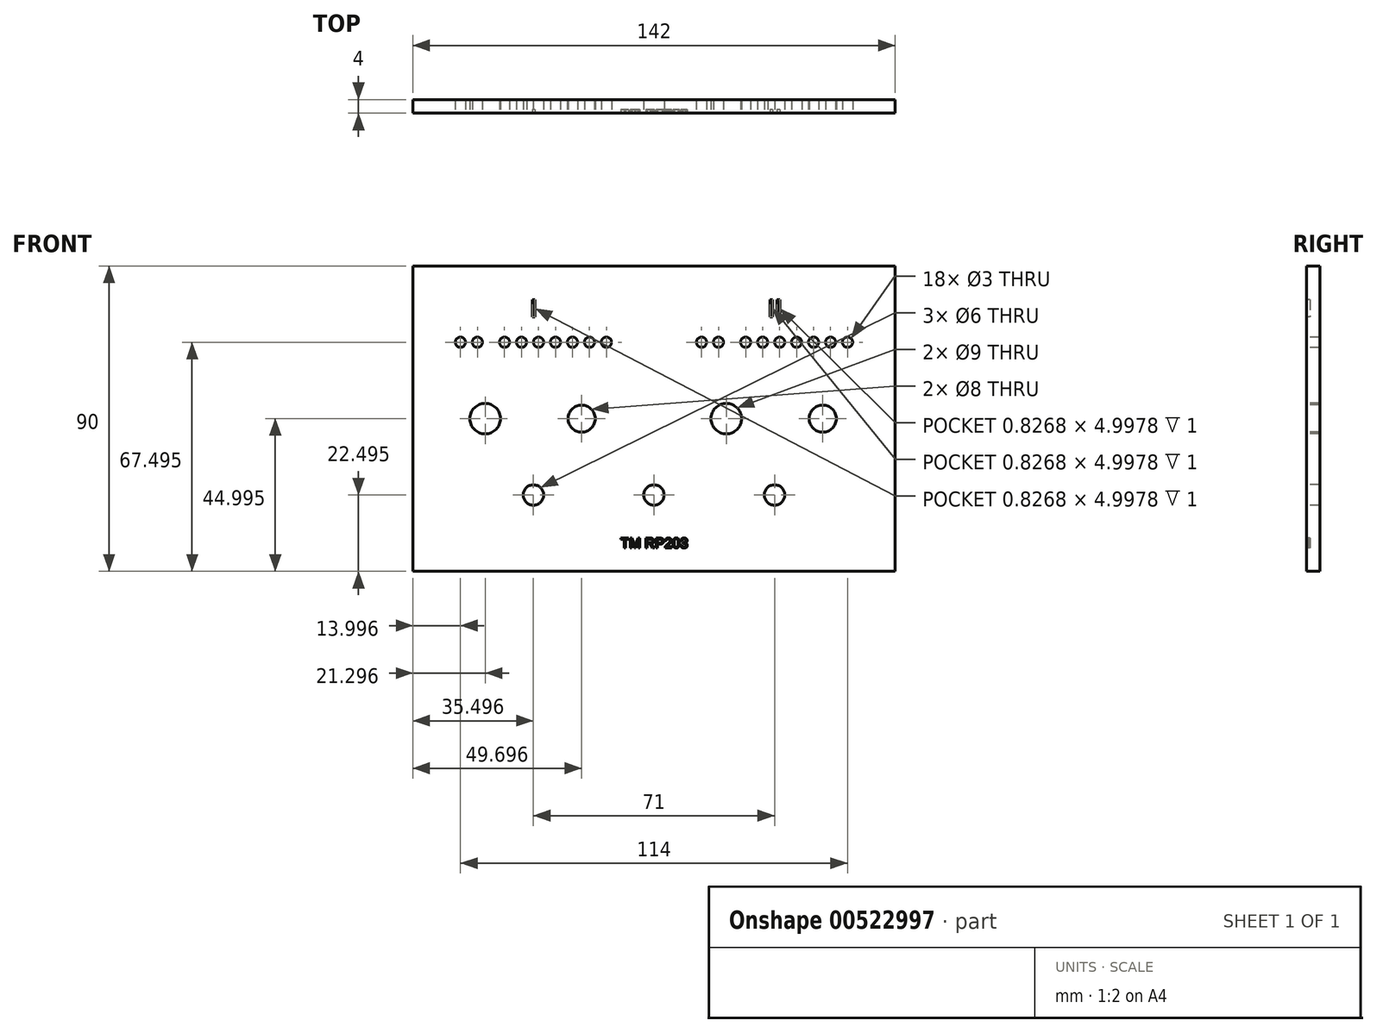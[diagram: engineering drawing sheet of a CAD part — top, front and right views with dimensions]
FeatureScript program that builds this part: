
annotation { "Feature Type Name" : "Feature", "Feature Type Description" : "" }
export const myFeature = defineFeature(function(context is Context, id is Id, definition is map)
    precondition{}
    {
        {
            var Q0;
            Q0=qCreatedBy(makeId("Front.planeOp"),FACE);
            var sketch = newSketch(context, id + "F0", { "sketchPlane" : qUnion([Q0])});
            skLineSegment(sketch, "E0.bottom", {"start": v(-71.11, 45.76) * mm, "end": v(70.89, 45.76) * mm});
            skLineSegment(sketch, "E0.top", {"start": v(-71.11, -44.24) * mm, "end": v(70.89, -44.24) * mm});
            skLineSegment(sketch, "E0.left", {"start": v(-71.11, 45.76) * mm, "end": v(-71.11, -44.24) * mm});
            skLineSegment(sketch, "E0.right", {"start": v(70.89, 45.76) * mm, "end": v(70.89, -44.24) * mm});
            skSolve(sketch);
        }
        {
            var Q0;
            Q0 = qSketchRegion(id + "F0", true);
            extrude(context, id + "F1", {"entities" : qUnion([Q0]), "depth" : 4 * mm, "offsetDistance" : 25 * mm});
        }
        {
            var Q0;
            Q0=makeQuery(id+"F1.opExtrude","CAP_FACE",FACE,{"disambiguationData":[OSD([sQuery(id+"F0.wireOp",EDGE,"E0.bottom"),sQuery(id+"F0.wireOp",EDGE,"E0.top"),sQuery(id+"F0.wireOp",EDGE,"E0.left"),sQuery(id+"F0.wireOp",EDGE,"E0.right")])],"isStart":false});
            var sketch = newSketch(context, id + "F2", { "sketchPlane" : qUnion([Q0])});
            skLineSegment(sketch, "E1", {"start": v(-71.11, 23.26) * mm, "end": v(70.89, 23.26) * mm, "construction": true});
            skLineSegment(sketch, "E2", {"start": v(-71.11, 0.76) * mm, "end": v(70.89, 0.76) * mm, "construction": true});
            skCircle(sketch, "E3", {"center": v(-49.81, 0.76) * mm, "radius": 4.5 * mm});
            skCircle(sketch, "E4", {"center": v(-21.41, 0.76) * mm, "radius": 4 * mm});
            skCircle(sketch, "E5", {"center": v(21.19, 0.76) * mm, "radius": 4.5 * mm});
            skCircle(sketch, "E6", {"center": v(49.59, 0.76) * mm, "radius": 4 * mm});
            skCircle(sketch, "E7", {"center": v(-49.81, 0.76) * mm, "radius": 13 * mm, "construction": true});
            skCircle(sketch, "E8", {"center": v(21.19, 0.76) * mm, "radius": 13 * mm, "construction": true});
            skCircle(sketch, "E9", {"center": v(-21.41, 0.76) * mm, "radius": 12 * mm, "construction": true});
            skCircle(sketch, "E10", {"center": v(49.59, 0.76) * mm, "radius": 12 * mm, "construction": true});
            skLineSegment(sketch, "E11", {"start": v(-71.11, -21.74) * mm, "end": v(70.89, -21.74) * mm, "construction": true});
            skCircle(sketch, "E12", {"center": v(-35.61, -21.74) * mm, "radius": 3 * mm});
            skCircle(sketch, "E13", {"center": v(35.39, -21.74) * mm, "radius": 3 * mm});
            skCircle(sketch, "E14", {"center": v(-57.11, 23.26) * mm, "radius": 1.5 * mm});
            skCircle(sketch, "E15", {"center": v(-52.11, 23.26) * mm, "radius": 1.5 * mm});
            skCircle(sketch, "E16", {"center": v(-44.11, 23.26) * mm, "radius": 1.5 * mm});
            skCircle(sketch, "E17", {"center": v(-39.11, 23.26) * mm, "radius": 1.5 * mm});
            skCircle(sketch, "E18", {"center": v(-34.11, 23.26) * mm, "radius": 1.5 * mm});
            skCircle(sketch, "E19", {"center": v(-29.11, 23.26) * mm, "radius": 1.5 * mm});
            skCircle(sketch, "E20", {"center": v(-24.11, 23.26) * mm, "radius": 1.5 * mm});
            skCircle(sketch, "E21", {"center": v(-19.11, 23.26) * mm, "radius": 1.5 * mm});
            skCircle(sketch, "E22", {"center": v(13.89, 23.26) * mm, "radius": 1.5 * mm});
            skCircle(sketch, "E23", {"center": v(18.89, 23.26) * mm, "radius": 1.5 * mm});
            skCircle(sketch, "E24", {"center": v(26.89, 23.26) * mm, "radius": 1.5 * mm});
            skCircle(sketch, "E25", {"center": v(31.89, 23.26) * mm, "radius": 1.5 * mm});
            skCircle(sketch, "E26", {"center": v(36.89, 23.26) * mm, "radius": 1.5 * mm});
            skCircle(sketch, "E27", {"center": v(41.89, 23.26) * mm, "radius": 1.5 * mm});
            skCircle(sketch, "E28", {"center": v(46.89, 23.26) * mm, "radius": 1.5 * mm});
            skCircle(sketch, "E29", {"center": v(51.89, 23.26) * mm, "radius": 1.5 * mm});
            skCircle(sketch, "E30", {"center": v(56.89, 23.26) * mm, "radius": 1.5 * mm});
            skCircle(sketch, "E31", {"center": v(-14.11, 23.26) * mm, "radius": 1.5 * mm});
            skCircle(sketch, "E32", {"center": v(-0.11, -21.74) * mm, "radius": 3 * mm});
            skSolve(sketch);
        }
        {
            var Q0;
            Q0 = qSketchRegion(id + "F2", true);
            extrude(context, id + "F3", {"entities" : qUnion([Q0]), "operationType" : NewBodyOperationType.REMOVE, "endBound" : BoundingType.THROUGH_ALL, "oppositeDirection" : true, "depth" : 25 * mm, "offsetDistance" : 25 * mm});
        }
        {
            var Q0;
            Q0=makeQuery(id+"F1.opExtrude","CAP_FACE",FACE,{"disambiguationData":[OSD([sQuery(id+"F0.wireOp",EDGE,"E0.bottom"),sQuery(id+"F0.wireOp",EDGE,"E0.top"),sQuery(id+"F0.wireOp",EDGE,"E0.left"),sQuery(id+"F0.wireOp",EDGE,"E0.right")])],"isStart":false});
            var sketch = newSketch(context, id + "F4", { "sketchPlane" : qUnion([Q0])});
            skText(sketch, "E33", { "text": "I", "fontName": "AllertaStencil-Regular.ttf"});
            skText(sketch, "E34", { "text": "II", "fontName": "AllertaStencil-Regular.ttf"});
            skText(sketch, "E35", { "text": "TM RP203", "fontName": "Arimo-Regular.ttf"});
            const initialGuessF4  = {"E33": [-0.03658, 0.03076, 1, 0, 0.005], "E34": [0.03338, 0.03076, 1, 0, 0.005], "E35": [-0.01, -0.03733, 1, 0, 0.003]};
            skSetInitialGuess(sketch, initialGuessF4);
            skSolve(sketch);
        }
        {
            var Q0;
            Q0 = qSketchRegion(id + "F4", true);
            extrude(context, id + "F5", {"entities" : qUnion([Q0]), "operationType" : NewBodyOperationType.REMOVE, "oppositeDirection" : true, "depth" : 1 * mm, "offsetDistance" : 25 * mm});
        }
    });
